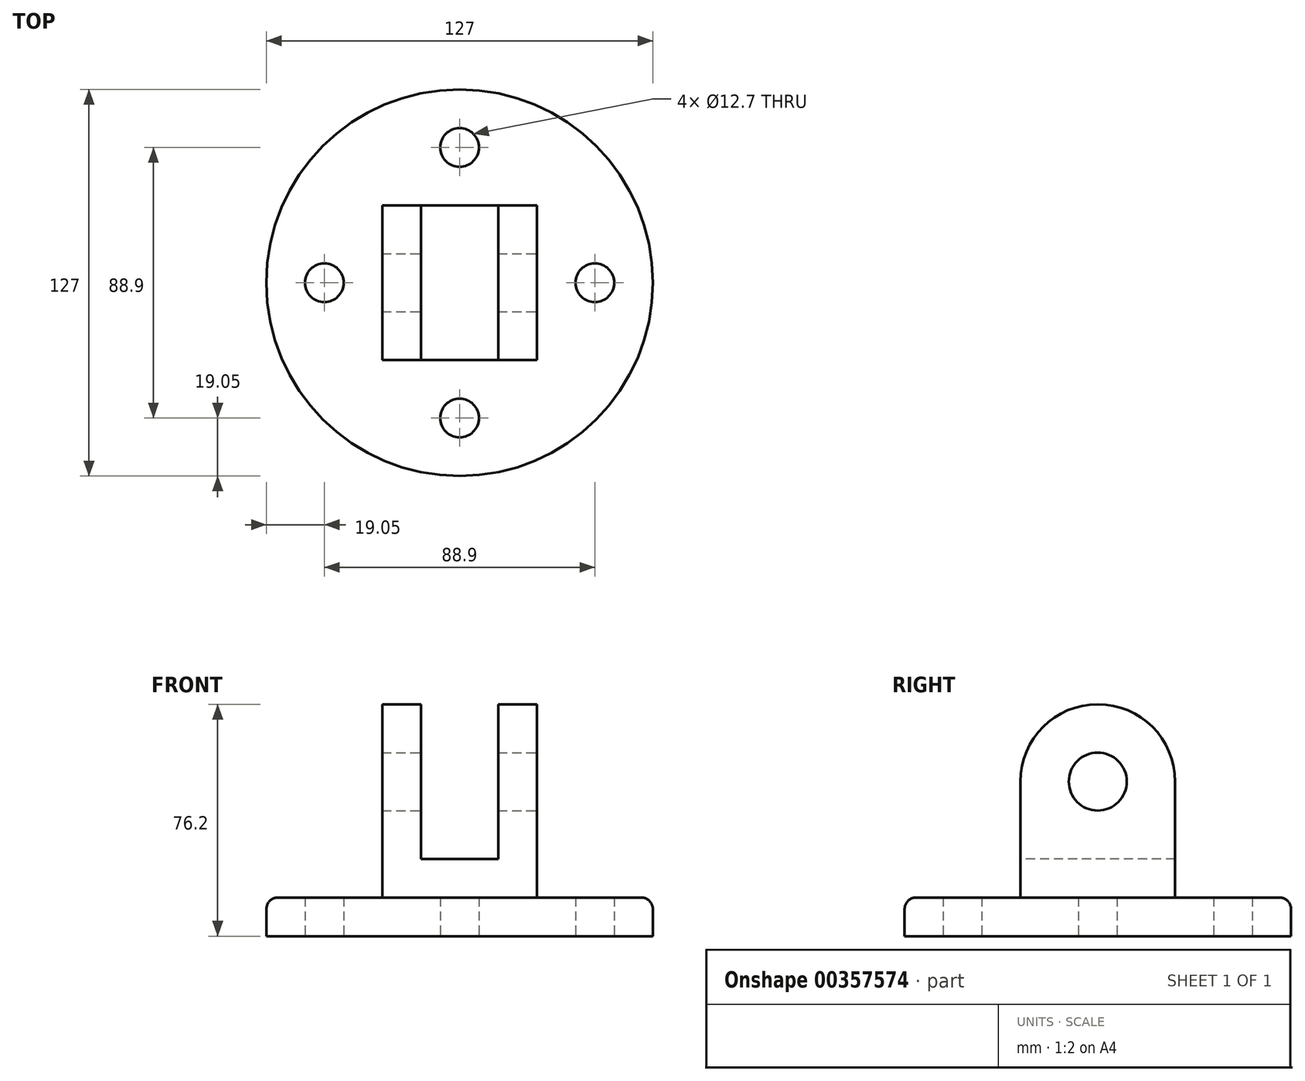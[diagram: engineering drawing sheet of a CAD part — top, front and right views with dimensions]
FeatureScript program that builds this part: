
annotation { "Feature Type Name" : "Feature", "Feature Type Description" : "" }
export const myFeature = defineFeature(function(context is Context, id is Id, definition is map)
    precondition{}
    {
        {
            var Q0;
            Q0=qCreatedBy(makeId("Top.planeOp"),FACE);
            var sketch = newSketch(context, id + "F0", { "sketchPlane" : qUnion([Q0])});
            skCircle(sketch, "E0", {"center": v(0, 0) * mm, "radius": 63.5 * mm});
            skCircle(sketch, "E1", {"center": v(0, 44.45) * mm, "radius": 6.35 * mm});
            skCircle(sketch, "E2", {"center": v(44.45, 0) * mm, "radius": 6.35 * mm});
            skCircle(sketch, "E3", {"center": v(0, -44.45) * mm, "radius": 6.35 * mm});
            skCircle(sketch, "E4", {"center": v(-44.45, 0) * mm, "radius": 6.35 * mm});
            skCircle(sketch, "E5", {"center": v(0, 0) * mm, "radius": 44.45 * mm, "construction": true});
            skSolve(sketch);
        }
        {
            var Q0;
            Q0 = qSketchRegion(id + "F0", true);
            extrude(context, id + "F1", {"entities" : qUnion([Q0]), "depth" : 12.7 * mm});
        }
        {
            var Q0;
            Q0=qCreatedBy(makeId("Right.planeOp"),FACE);
            var sketch = newSketch(context, id + "F2", { "sketchPlane" : qUnion([Q0])});
            skLineSegment(sketch, "E6", {"start": v(-25.4, 12.7) * mm, "end": v(-25.4, 50.8) * mm});
            skLineSegment(sketch, "E7", {"start": v(25.4, 50.8) * mm, "end": v(25.4, 12.7) * mm});
            skCircle(sketch, "E8", {"center": v(0, 50.8) * mm, "radius": 9.53 * mm});
            skPoint(sketch, "E9.visualSharp", {"position": v(-25.4, 81.35) * mm});
            skPoint(sketch, "E10.visualSharp", {"position": v(25.4, 81.35) * mm});
            skArc(sketch, "E10.filletArc", {"start": v(25.4, 50.8) * mm, "mid": v(0, 76.2) * mm, "end": v(-25.4, 50.8) * mm});
            skLineSegment(sketch, "E11", {"start": v(-25.4, 12.7) * mm, "end": v(25.4, 12.7) * mm});
            skSolve(sketch);
        }
        {
            var Q0;
            Q0 = qSketchRegion(id + "F2", true);
            extrude(context, id + "F3", {"entities" : qUnion([Q0]), "operationType" : NewBodyOperationType.ADD, "endBound" : BoundingType.SYMMETRIC, "oppositeDirection" : true, "depth" : 50.8 * mm});
        }
        {
            var Q0;
            Q0=makeQuery(id+"F3.opExtrude","SWEPT_FACE",FACE,{"disambiguationData":[OSD([sQuery(id+"F2.wireOp",EDGE,"E6")])]});
            var sketch = newSketch(context, id + "F4", { "sketchPlane" : qUnion([Q0])});
            skLineSegment(sketch, "E12.bottom", {"start": v(-12.7, 25.4) * mm, "end": v(12.7, 25.4) * mm});
            skLineSegment(sketch, "E12.top", {"start": v(-12.7, 76.2) * mm, "end": v(12.7, 76.2) * mm});
            skLineSegment(sketch, "E12.left", {"start": v(-12.7, 25.4) * mm, "end": v(-12.7, 76.2) * mm});
            skLineSegment(sketch, "E12.right", {"start": v(12.7, 25.4) * mm, "end": v(12.7, 76.2) * mm});
            skSolve(sketch);
        }
        {
            var Q0;
            Q0 = qSketchRegion(id + "F4", true);
            extrude(context, id + "F5", {"entities" : qUnion([Q0]), "operationType" : NewBodyOperationType.REMOVE, "endBound" : BoundingType.THROUGH_ALL, "oppositeDirection" : true, "depth" : 25.4 * mm});
        }
        {
            var Q0;
            Q0=makeQuery(id+"F3.opExtrude","SWEPT_EDGE",EDGE,{"disambiguationData":[OSD([sQuery(id+"F2.wireOp",EDGE,"E6"),sQuery(id+"F2.wireOp",EDGE,"E11")])]});
            var Q1;
            Q1=makeQuery(id+"F3.opExtrude","CAP_EDGE",EDGE,{"disambiguationData":[OSD([sQuery(id+"F2.wireOp",EDGE,"E11")])],"isStart":true});
            var Q2;
            Q2=makeQuery(id+"F3.opExtrude","SWEPT_EDGE",EDGE,{"disambiguationData":[OSD([sQuery(id+"F2.wireOp",EDGE,"E7"),sQuery(id+"F2.wireOp",EDGE,"E11")])]});
            var Q3;
            Q3=makeQuery(id+"F3.opExtrude","CAP_EDGE",EDGE,{"disambiguationData":[OSD([sQuery(id+"F2.wireOp",EDGE,"E11")])],"isStart":false});
            var Q4;
            Q4=makeQuery(id+"F1.opExtrude","CAP_EDGE",EDGE,{"disambiguationData":[OSD([sQuery(id+"F0.wireOp",EDGE,"E0")])],"isStart":false});
            fillet(context, id + "F6", {"entities" : qUnion([Q0, Q1, Q2, Q3, Q4]), "radius" : 3.8 * mm, "tangentPropagation" : true, "allowEdgeOverflow" : false});
        }
    });
